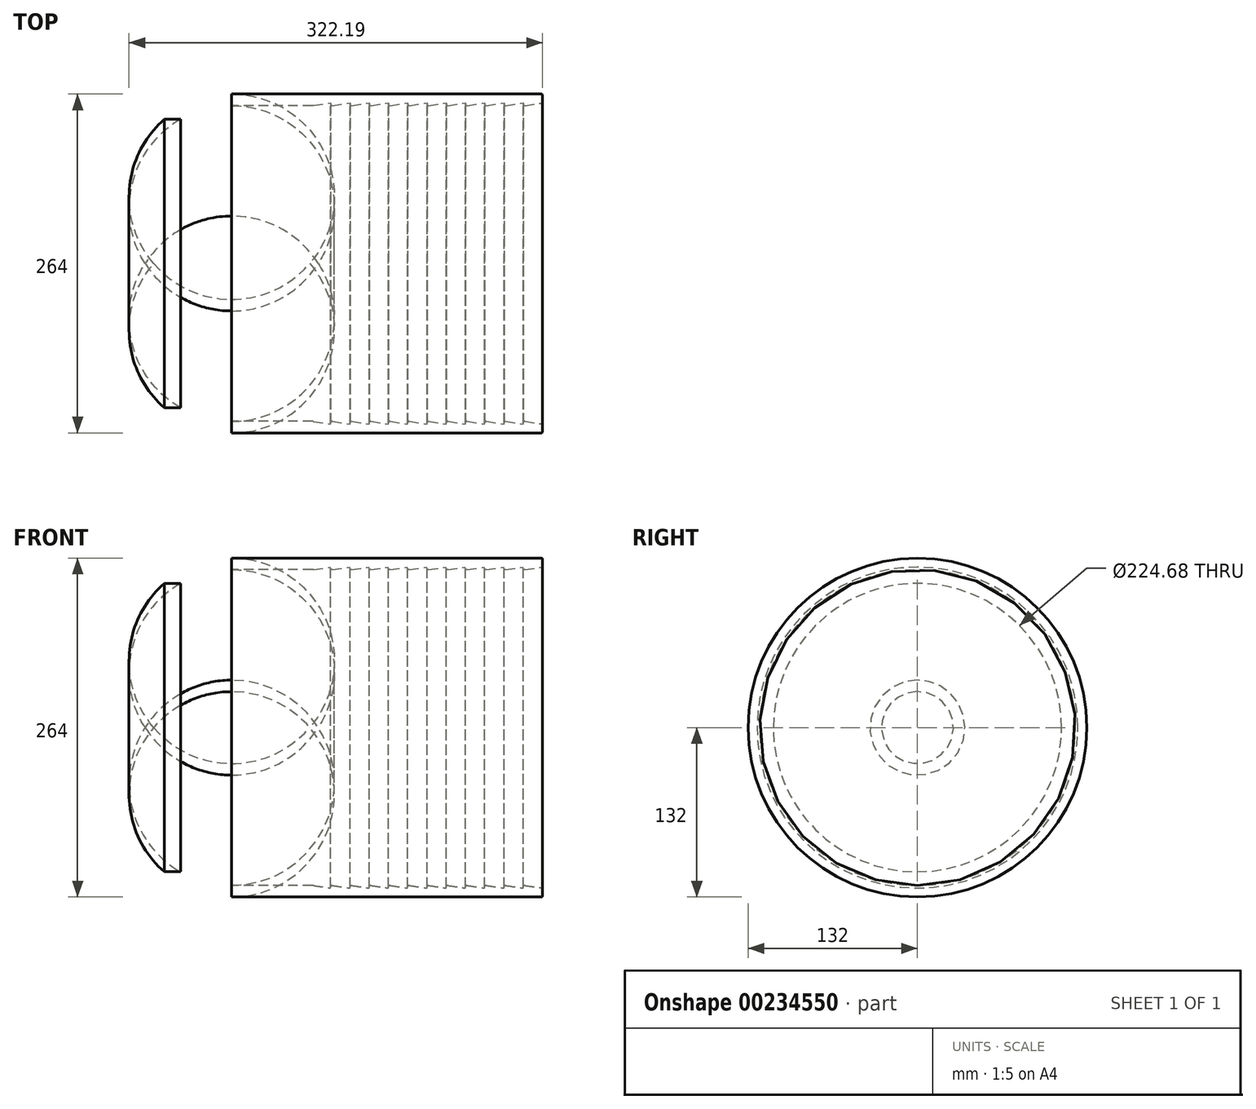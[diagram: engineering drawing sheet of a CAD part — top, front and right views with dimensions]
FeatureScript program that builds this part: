
annotation { "Feature Type Name" : "Feature", "Feature Type Description" : "" }
export const myFeature = defineFeature(function(context is Context, id is Id, definition is map)
    precondition{}
    {
        {
            var Q0;
            Q0=qCreatedBy(makeId("Front.planeOp"),FACE);
            var sketch = newSketch(context, id + "F0", { "sketchPlane" : qUnion([Q0])});
            skLineSegment(sketch, "E0", {"start": v(-1, 132) * mm, "end": v(-242.18, 132) * mm});
            skLineSegment(sketch, "E1", {"start": v(0, 131) * mm, "end": v(0, 125.87) * mm});
            skLineSegment(sketch, "E2", {"start": v(-0.86, 124.88) * mm, "end": v(-13.86, 123.01) * mm});
            skLineSegment(sketch, "E3", {"start": v(-15, 124) * mm, "end": v(-15, 125) * mm});
            skPoint(sketch, "E4.visualSharp", {"position": v(-15, 122.85) * mm});
            skArc(sketch, "E4.filletArc", {"start": v(-15, 124) * mm, "mid": v(-14.65, 123.24) * mm, "end": v(-13.86, 123.01) * mm});
            skLineSegment(sketch, "E5", {"start": v(-179, 123) * mm, "end": v(34.73, 123) * mm, "construction": true});
            skLineSegment(sketch, "E6.1.0.0", {"start": v(-15, 125) * mm, "end": v(-28.86, 123.01) * mm});
            skArc(sketch, "E6.1.0.1", {"start": v(-30, 124) * mm, "mid": v(-29.65, 123.24) * mm, "end": v(-28.86, 123.01) * mm});
            skLineSegment(sketch, "E6.1.0.2", {"start": v(-30, 124) * mm, "end": v(-30, 125) * mm});
            skLineSegment(sketch, "E6.2.0.0", {"start": v(-30, 125) * mm, "end": v(-43.86, 123.01) * mm});
            skArc(sketch, "E6.2.0.1", {"start": v(-45, 124) * mm, "mid": v(-44.65, 123.24) * mm, "end": v(-43.86, 123.01) * mm});
            skLineSegment(sketch, "E6.2.0.2", {"start": v(-45, 124) * mm, "end": v(-45, 125) * mm});
            skLineSegment(sketch, "E6.3.0.0", {"start": v(-45, 125) * mm, "end": v(-58.86, 123.01) * mm});
            skArc(sketch, "E6.3.0.1", {"start": v(-60, 124) * mm, "mid": v(-59.65, 123.24) * mm, "end": v(-58.86, 123.01) * mm});
            skLineSegment(sketch, "E6.3.0.2", {"start": v(-60, 124) * mm, "end": v(-60, 125) * mm});
            skLineSegment(sketch, "E6.4.0.0", {"start": v(-60, 125) * mm, "end": v(-73.86, 123.01) * mm});
            skArc(sketch, "E6.4.0.1", {"start": v(-75, 124) * mm, "mid": v(-74.65, 123.24) * mm, "end": v(-73.86, 123.01) * mm});
            skLineSegment(sketch, "E6.4.0.2", {"start": v(-75, 124) * mm, "end": v(-75, 125) * mm});
            skLineSegment(sketch, "E6.5.0.0", {"start": v(-75, 125) * mm, "end": v(-88.86, 123.01) * mm});
            skArc(sketch, "E6.5.0.1", {"start": v(-90, 124) * mm, "mid": v(-89.65, 123.24) * mm, "end": v(-88.86, 123.01) * mm});
            skLineSegment(sketch, "E6.5.0.2", {"start": v(-90, 124) * mm, "end": v(-90, 125) * mm});
            skLineSegment(sketch, "E6.6.0.0", {"start": v(-90, 125) * mm, "end": v(-103.86, 123.01) * mm});
            skArc(sketch, "E6.6.0.1", {"start": v(-105, 124) * mm, "mid": v(-104.65, 123.24) * mm, "end": v(-103.86, 123.01) * mm});
            skLineSegment(sketch, "E6.6.0.2", {"start": v(-105, 124) * mm, "end": v(-105, 125) * mm});
            skLineSegment(sketch, "E6.7.0.0", {"start": v(-105, 125) * mm, "end": v(-118.86, 123.01) * mm});
            skArc(sketch, "E6.7.0.1", {"start": v(-120, 124) * mm, "mid": v(-119.65, 123.24) * mm, "end": v(-118.86, 123.01) * mm});
            skLineSegment(sketch, "E6.7.0.2", {"start": v(-120, 124) * mm, "end": v(-120, 125) * mm});
            skLineSegment(sketch, "E6.8.0.0", {"start": v(-120, 125) * mm, "end": v(-133.86, 123.01) * mm});
            skArc(sketch, "E6.8.0.1", {"start": v(-135, 124) * mm, "mid": v(-134.65, 123.24) * mm, "end": v(-133.86, 123.01) * mm});
            skLineSegment(sketch, "E6.8.0.2", {"start": v(-135, 124) * mm, "end": v(-135, 125) * mm});
            skLineSegment(sketch, "E6.9.0.0", {"start": v(-135, 125) * mm, "end": v(-148.86, 123.01) * mm});
            skArc(sketch, "E6.9.0.1", {"start": v(-150, 124) * mm, "mid": v(-149.65, 123.24) * mm, "end": v(-148.86, 123.01) * mm});
            skLineSegment(sketch, "E6.9.0.2", {"start": v(-150, 124) * mm, "end": v(-150, 125) * mm});
            skLineSegment(sketch, "E6.10.0.0", {"start": v(-150, 125) * mm, "end": v(-163.86, 123.01) * mm});
            skArc(sketch, "E6.10.0.1", {"start": v(-165, 124) * mm, "mid": v(-164.65, 123.24) * mm, "end": v(-163.86, 123.01) * mm});
            skLineSegment(sketch, "E6.10.0.2", {"start": v(-165, 124) * mm, "end": v(-165, 125) * mm});
            skLineSegment(sketch, "E6.11.0.0", {"start": v(-165, 125) * mm, "end": v(-178.57, 123.05) * mm});
            skArc(sketch, "E6.11.0.1", {"start": v(-179, 125) * mm, "mid": v(-180, 123.93) * mm, "end": v(-178.86, 123.01) * mm});
            skLineSegment(sketch, "E6.direction1", {"start": v(-13.86, 123.01) * mm, "end": v(-28.86, 123.01) * mm, "construction": true});
            skPoint(sketch, "E7.visualSharp", {"position": v(0, 132) * mm});
            skArc(sketch, "E7.filletArc", {"start": v(0, 131) * mm, "mid": v(-0.3, 131.7) * mm, "end": v(-1, 132) * mm});
            skPoint(sketch, "E8.visualSharp", {"position": v(0, 125) * mm});
            skArc(sketch, "E8.filletArc", {"start": v(-0.86, 124.88) * mm, "mid": v(-0.24, 125.21) * mm, "end": v(0, 125.87) * mm});
            skLineSegment(sketch, "E9", {"start": v(-242.18, 123.01) * mm, "end": v(-179.29, 123) * mm});
            skPoint(sketch, "E10.newPointA", {"position": v(-178.86, 123.01) * mm});
            skArc(sketch, "E10.filletArc", {"start": v(-179.29, 123) * mm, "mid": v(-178.93, 123.01) * mm, "end": v(-178.57, 123.05) * mm});
            skArc(sketch, "E11", {"start": v(-242.18, 132) * mm, "mid": v(-270.22, 126.92) * mm, "end": v(-294.7, 112.34) * mm});
            skArc(sketch, "E12", {"start": v(-242.18, 123.01) * mm, "mid": v(-262.85, 120.3) * mm, "end": v(-282.1, 112.34) * mm});
            skLineSegment(sketch, "E13", {"start": v(-282.1, 112.34) * mm, "end": v(-294.7, 112.34) * mm});
            skLineSegment(sketch, "E14", {"start": v(-242.18, 123.01) * mm, "end": v(-242.18, 140.99) * mm});
            skLineSegment(sketch, "E15", {"start": v(0, 0) * mm, "end": v(-305.6, 0) * mm, "construction": true});
            skSolve(sketch);
        }
        {
            var Q0;
            {var subQ0=sQuery(id+"F0.wireOp",EDGE,"E0");Q0=makeQuery(id+"F0.imprint","IMPRINT",FACE,{"disambiguationData":[TD([[makeQuery(id+"F0.imprint","IMPRINT",EDGE,{"derivedFrom":subQ0}),1.0]])]});}
            var Q1;
            {var subQ0=sQuery(id+"F0.wireOp",EDGE,"E11");Q1=makeQuery(id+"F0.imprint","IMPRINT",FACE,{"disambiguationData":[TD([[makeQuery(id+"F0.imprint","IMPRINT",EDGE,{"derivedFrom":subQ0}),1.0]])]});}
            var Q2;
            Q2=sQuery(id+"F0.wireOp",EDGE,"E15");
            revolve(context, id + "F1", {"entities" : qUnion([Q0, Q1]), "axis" : qUnion([Q2]), "revolveType" : RevolveType.FULL});
        }
    });
